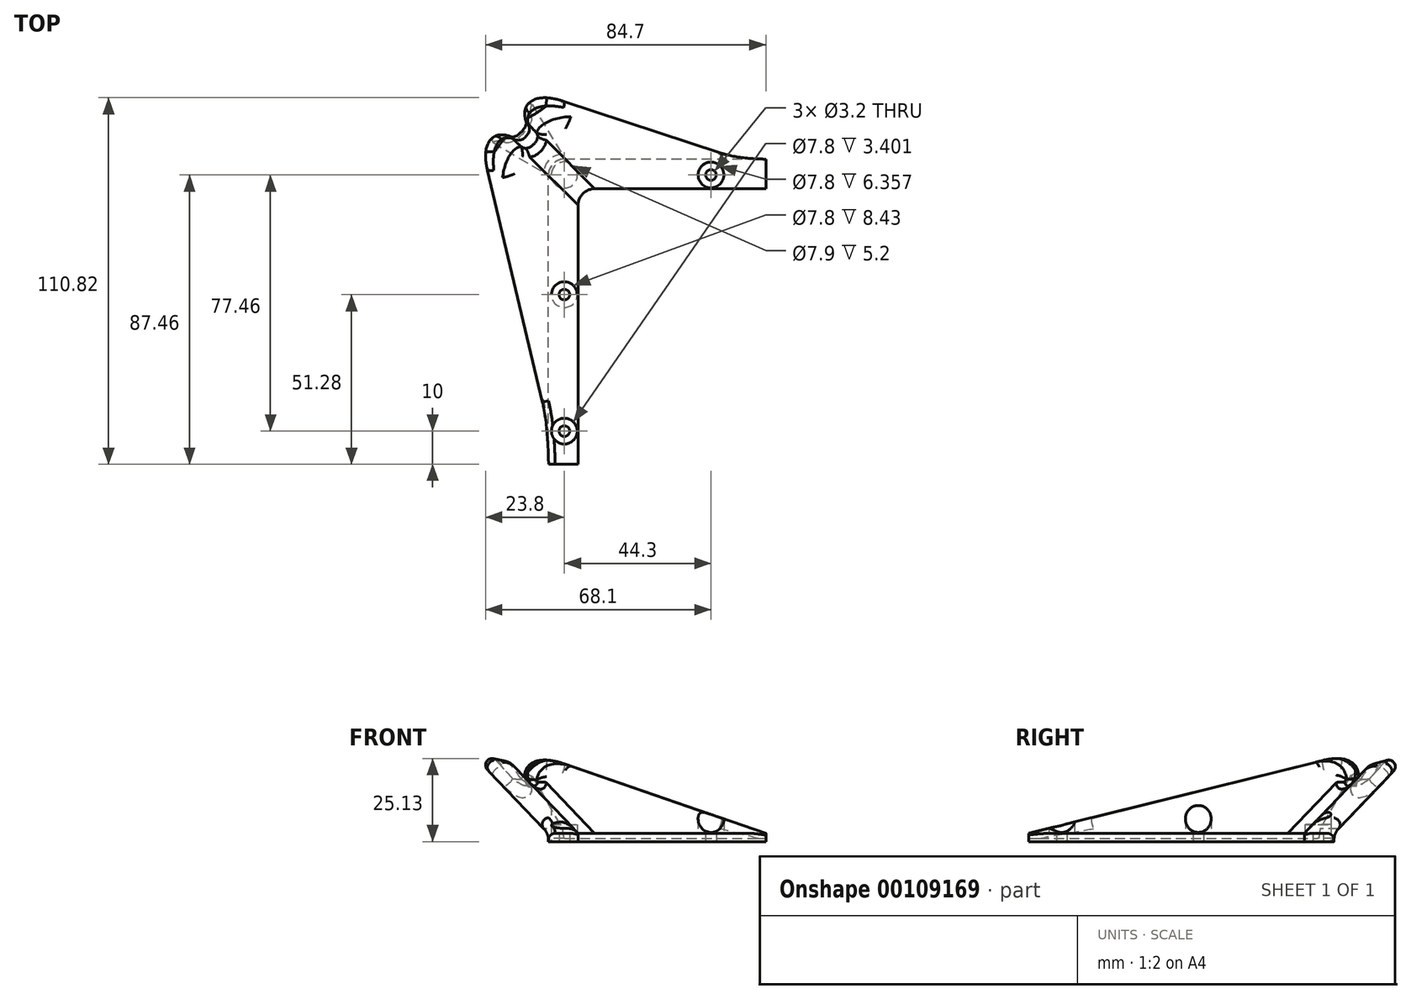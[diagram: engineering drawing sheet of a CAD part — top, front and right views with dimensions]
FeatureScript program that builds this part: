
annotation { "Feature Type Name" : "Feature", "Feature Type Description" : "" }
export const myFeature = defineFeature(function(context is Context, id is Id, definition is map)
    precondition{}
    {
        {
            var Q0;
            Q0=qCreatedBy(makeId("Top.planeOp"),FACE);
            var sketch = newSketch(context, id + "F0", { "sketchPlane" : qUnion([Q0])});
            skLineSegment(sketch, "E0", {"start": v(5, 0) * mm, "end": v(65.74, 0) * mm});
            skLineSegment(sketch, "E1", {"start": v(65.74, 0) * mm, "end": v(65.74, -9) * mm});
            skLineSegment(sketch, "E2", {"start": v(65.74, -9) * mm, "end": v(14, -9) * mm});
            skLineSegment(sketch, "E3", {"start": v(9, -14) * mm, "end": v(9, -92.3) * mm});
            skLineSegment(sketch, "E4", {"start": v(9, -92.3) * mm, "end": v(0, -92.3) * mm});
            skLineSegment(sketch, "E5", {"start": v(0, -92.3) * mm, "end": v(0, -5) * mm});
            skPoint(sketch, "E6.visualSharp", {"position": v(9, -9) * mm});
            skArc(sketch, "E6.filletArc", {"start": v(14, -9) * mm, "mid": v(10.46, -10.46) * mm, "end": v(9, -14) * mm});
            skPoint(sketch, "E7.visualSharp", {"position": v(0, 0) * mm});
            skArc(sketch, "E7.filletArc", {"start": v(5, 0) * mm, "mid": v(1.46, -1.46) * mm, "end": v(0, -5) * mm});
            skLineSegment(sketch, "E8", {"start": v(0, 0) * mm, "end": v(9, -9) * mm, "construction": true});
            skCircle(sketch, "E9", {"center": v(4.84, -4.84) * mm, "radius": 1.6 * mm});
            skCircle(sketch, "E10", {"center": v(49.14, -4.84) * mm, "radius": 1.6 * mm});
            skCircle(sketch, "E11", {"center": v(4.84, -41.02) * mm, "radius": 1.6 * mm});
            skCircle(sketch, "E12", {"center": v(4.84, -82.3) * mm, "radius": 1.6 * mm});
            skLineSegment(sketch, "E13", {"start": v(4.84, -92.3) * mm, "end": v(4.84, -4.84) * mm, "construction": true});
            skLineSegment(sketch, "E14", {"start": v(4.84, -4.84) * mm, "end": v(65.74, -4.84) * mm, "construction": true});
            skSolve(sketch);
        }
        {
            var Q0;
            Q0 = qSketchRegion(id + "F0", true);
            extrude(context, id + "F1", {"entities" : qUnion([Q0]), "depth" : 1.5 * mm});
        }
        {
            var Q0;
            Q0=qCreatedBy(makeId("Top.planeOp"),FACE);
            cPlane(context, id + "F2", {"entities" : qUnion([Q0]), "cplaneType" : CPlaneType.OFFSET, "offset" : 25 * mm, "width" : 150 * mm, "height" : 150 * mm});
        }
        {
            var Q0;
            Q0=qCreatedBy(id+"F2.planeOp",FACE);
            var sketch = newSketch(context, id + "F3", { "sketchPlane" : qUnion([Q0])});
            skLineSegment(sketch, "E15", {"start": v(0, 0) * mm, "end": v(-11.16, 11.16) * mm, "construction": true});
            skSolve(sketch);
        }
        {
            var Q0;
            Q0=makeQuery(id+"F1.opExtrude","CAP_FACE",FACE,{"disambiguationData":[OSD([sQuery(id+"F0.wireOp",EDGE,"E0"),sQuery(id+"F0.wireOp",EDGE,"E1"),sQuery(id+"F0.wireOp",EDGE,"E2"),sQuery(id+"F0.wireOp",EDGE,"E3"),sQuery(id+"F0.wireOp",EDGE,"E4"),sQuery(id+"F0.wireOp",EDGE,"E5"),sQuery(id+"F0.wireOp",EDGE,"E6.filletArc"),sQuery(id+"F0.wireOp",EDGE,"E7.filletArc"),sQuery(id+"F0.wireOp",EDGE,"E9"),sQuery(id+"F0.wireOp",EDGE,"E10"),sQuery(id+"F0.wireOp",EDGE,"E11"),sQuery(id+"F0.wireOp",EDGE,"E12")])],"isStart":false});
            var sketch = newSketch(context, id + "F4", { "sketchPlane" : qUnion([Q0])});
            skLineSegment(sketch, "E16.0", {"start": v(5, 0) * mm, "end": v(65.74, 0) * mm});
            skArc(sketch, "E16.1", {"start": v(5, 0) * mm, "mid": v(1.46, -1.46) * mm, "end": v(0, -5) * mm});
            skLineSegment(sketch, "E16.2", {"start": v(0, -92.3) * mm, "end": v(0, -5) * mm});
            skLineSegment(sketch, "E16.3", {"start": v(9, -14) * mm, "end": v(9, -92.3) * mm});
            skArc(sketch, "E16.4", {"start": v(14, -9) * mm, "mid": v(10.46, -10.46) * mm, "end": v(9, -14) * mm});
            skLineSegment(sketch, "E16.5", {"start": v(65.74, -9) * mm, "end": v(14, -9) * mm});
            skLineSegment(sketch, "E16.6", {"start": v(65.74, 0) * mm, "end": v(65.74, -9) * mm});
            skLineSegment(sketch, "E16.7", {"start": v(9, -92.3) * mm, "end": v(0, -92.3) * mm});
            skSolve(sketch);
        }
        {
            var Q0;
            Q0=qCreatedBy(id+"F2.planeOp",FACE);
            var sketch = newSketch(context, id + "F5", { "sketchPlane" : qUnion([Q0])});
            skLineSegment(sketch, "E17", {"start": v(-8.47, 13.47) * mm, "end": v(-2.47, 13.47) * mm});
            skLineSegment(sketch, "E18", {"start": v(-13.47, 8.47) * mm, "end": v(-13.47, 2.47) * mm});
            skLineSegment(sketch, "E19", {"start": v(-2.47, 22.47) * mm, "end": v(-8.47, 22.47) * mm});
            skLineSegment(sketch, "E20", {"start": v(-22.47, 8.47) * mm, "end": v(-22.47, 2.47) * mm});
            skLineSegment(sketch, "E21", {"start": v(-22.47, 2.47) * mm, "end": v(-13.47, 2.47) * mm});
            skLineSegment(sketch, "E22", {"start": v(-2.47, 22.47) * mm, "end": v(-2.47, 13.47) * mm});
            skPoint(sketch, "E23.visualSharp", {"position": v(-13.47, 13.47) * mm});
            skArc(sketch, "E23.filletArc", {"start": v(-8.47, 13.47) * mm, "mid": v(-12, 12) * mm, "end": v(-13.47, 8.47) * mm});
            skPoint(sketch, "E24.visualSharp", {"position": v(-22.47, 22.47) * mm});
            skArc(sketch, "E24.filletArc", {"start": v(-8.47, 22.47) * mm, "mid": v(-18.37, 18.37) * mm, "end": v(-22.47, 8.47) * mm});
            skSolve(sketch);
        }
        {
            var Q1;
            Q1 = qSketchRegion(id + "F5", true);
            var Q2;
            Q2 = qSketchRegion(id + "F4", true);
            loft(context, id + "F6", {"operationType" : NewBodyOperationType.ADD, "sheetProfilesArray" : [{ "sheetProfileEntities" : qUnion([Q1]) }, { "sheetProfileEntities" : qUnion([Q2]) }]});
        }
        {
            var Q0;
            Q0=makeQuery(id+"F6.opLoft","MID_CAP_EDGE",EDGE,{"disambiguationData":[OSD([sQuery(id+"F5.wireOp",EDGE,"E18"),sQuery(id+"F5.wireOp",EDGE,"E20"),sQuery(id+"F5.wireOp",EDGE,"E21")])],"capPos":0.0});
            var Q1;
            Q1=makeQuery(id+"F6.opLoft","MID_CAP_EDGE",EDGE,{"disambiguationData":[OSD([sQuery(id+"F5.wireOp",EDGE,"E17"),sQuery(id+"F5.wireOp",EDGE,"E19"),sQuery(id+"F5.wireOp",EDGE,"E22")])],"capPos":0.0});
            fillet(context, id + "F7", {"entities" : qUnion([Q0, Q1]), "radius" : 30 * mm, "tangentPropagation" : true, "allowEdgeOverflow" : false});
        }
        {
            var Q0;
            Q0=makeQuery(id+"F6.boolean.opBoolean","MERGE",EDGE,{"derivedFrom":[makeQuery(id+"F1.opExtrude","CAP_EDGE",EDGE,{"disambiguationData":[OSD([sQuery(id+"F0.wireOp",EDGE,"E5")])],"isStart":false}),makeQuery(id+"F6.opLoft","MID_CAP_EDGE",EDGE,{"disambiguationData":[OSD([sQuery(id+"F4.wireOp",EDGE,"E16.1"),sQuery(id+"F4.wireOp",EDGE,"E16.2"),sQuery(id+"F4.wireOp",EDGE,"E16.7")])],"capPos":1.0})]});
            fillet(context, id + "F8", {"entities" : qUnion([Q0]), "radius" : 5 * mm, "tangentPropagation" : true, "allowEdgeOverflow" : false});
        }
        {
            var Q0;
            Q0=sQuery(id+"F3.wireOp",EDGE,"E15");
            var Q1;
            Q1=sQuery(id+"F3.wireOp",VERTEX,"E15.end");
            cPlane(context, id + "F9", {"entities" : qUnion([Q0, Q1]), "cplaneType" : CPlaneType.LINE_POINT, "offset" : 25 * mm, "width" : 150 * mm, "height" : 150 * mm});
        }
        {
            var Q0;
            Q0=qCreatedBy(id+"F9.planeOp",FACE);
            var sketch = newSketch(context, id + "F10", { "sketchPlane" : qUnion([Q0])});
            skArc(sketch, "E25", {"start": v(-3.54, 19.4) * mm, "mid": v(0, 15.86) * mm, "end": v(3.54, 19.4) * mm});
            skLineSegment(sketch, "E26", {"start": v(3.54, 19.4) * mm, "end": v(3.54, 37.26) * mm});
            skLineSegment(sketch, "E27", {"start": v(-3.54, 19.4) * mm, "end": v(-3.54, 37.26) * mm});
            skLineSegment(sketch, "E28", {"start": v(-3.54, 37.26) * mm, "end": v(3.54, 37.26) * mm});
            skSolve(sketch);
        }
        {
            var Q0;
            Q0 = qSketchRegion(id + "F10", true);
            extrude(context, id + "F11", {"entities" : qUnion([Q0]), "operationType" : NewBodyOperationType.REMOVE, "endBound" : BoundingType.SYMMETRIC, "oppositeDirection" : true, "depth" : 25 * mm});
        }
        {
            var Q0;
            Q0=makeQuery(id+"F11.boolean.opBoolean","INTERSECT",EDGE,{"derivedFrom":[makeQuery(id+"F6.opLoft","CAP_FACE",FACE,{"disambiguationData":[OSD([makeQuery(id+"F5.imprint","IMPRINT",FACE,{"disambiguationData":[TD([[makeQuery(id+"F5.imprint","IMPRINT",EDGE,{"derivedFrom":sQuery(id+"F5.wireOp",EDGE,"E17")}),1.0]])]})])],"isStart":true}),makeQuery(id+"F11.opExtrude","SWEPT_FACE",FACE,{"disambiguationData":[OSD([sQuery(id+"F10.wireOp",EDGE,"E26")])]})]});
            var Q1;
            Q1=makeQuery(id+"F11.boolean.opBoolean","INTERSECT",EDGE,{"derivedFrom":[makeQuery(id+"F6.opLoft","CAP_FACE",FACE,{"disambiguationData":[OSD([makeQuery(id+"F5.imprint","IMPRINT",FACE,{"disambiguationData":[TD([[makeQuery(id+"F5.imprint","IMPRINT",EDGE,{"derivedFrom":sQuery(id+"F5.wireOp",EDGE,"E17")}),1.0]])]})])],"isStart":true}),makeQuery(id+"F11.opExtrude","SWEPT_FACE",FACE,{"disambiguationData":[OSD([sQuery(id+"F10.wireOp",EDGE,"E27")])]})]});
            fillet(context, id + "F12", {"entities" : qUnion([Q0, Q1]), "radius" : 10 * mm, "tangentPropagation" : true, "allowEdgeOverflow" : false});
        }
        {
            var Q0;
            Q0=makeQuery(id+"F11.boolean.opBoolean","INTERSECT",EDGE,{"derivedFrom":[makeQuery(id+"F6.opLoft","SWEPT_FACE",FACE,{"disambiguationData":[OSD([sQuery(id+"F4.wireOp",EDGE,"E16.3"),sQuery(id+"F4.wireOp",EDGE,"E16.4"),sQuery(id+"F4.wireOp",EDGE,"E16.5"),sQuery(id+"F5.wireOp",EDGE,"E17"),sQuery(id+"F5.wireOp",EDGE,"E18"),sQuery(id+"F5.wireOp",EDGE,"E23.filletArc")])]}),makeQuery(id+"F11.opExtrude","SWEPT_FACE",FACE,{"disambiguationData":[OSD([sQuery(id+"F10.wireOp",EDGE,"E25")])]})]});
            fillet(context, id + "F13", {"entities" : qUnion([Q0]), "radius" : 5 * mm, "tangentPropagation" : true, "allowEdgeOverflow" : false});
        }
        {
            var Q0;
            {var subQ0=sQuery(id+"F5.wireOp",EDGE,"E24.filletArc");var subQ1=sQuery(id+"F5.wireOp",EDGE,"E20");var subQ2=sQuery(id+"F5.wireOp",EDGE,"E19");Q0=makeQuery(id+"F12.opFillet","BLEND_EDGE",EDGE,{"blendedFrom":[makeQuery(id+"F11.boolean.opBoolean","INTERSECT",EDGE,{"derivedFrom":[makeQuery(id+"F6.opLoft","CAP_FACE",FACE,{"disambiguationData":[OSD([makeQuery(id+"F5.imprint","IMPRINT",FACE,{"disambiguationData":[TD([[makeQuery(id+"F5.imprint","IMPRINT",EDGE,{"derivedFrom":sQuery(id+"F5.wireOp",EDGE,"E17")}),1.0]])]})])],"isStart":true}),makeQuery(id+"F11.opExtrude","SWEPT_FACE",FACE,{"disambiguationData":[OSD([sQuery(id+"F10.wireOp",EDGE,"E26")])]})]}),makeQuery(id+"F6.opLoft","SWEPT_FACE",FACE,{"disambiguationData":[OSD([sQuery(id+"F4.wireOp",EDGE,"E16.0"),sQuery(id+"F4.wireOp",EDGE,"E16.1"),sQuery(id+"F4.wireOp",EDGE,"E16.2"),subQ2,subQ1,subQ0])]})],"blendedInto":[makeQuery(id+"F6.opLoft","SWEPT_FACE",FACE,{"disambiguationData":[OSD([sQuery(id+"F4.wireOp",EDGE,"E16.0"),sQuery(id+"F4.wireOp",EDGE,"E16.1"),sQuery(id+"F4.wireOp",EDGE,"E16.2"),subQ2,subQ1,subQ0])]})]});}
            fillet(context, id + "F14", {"entities" : qUnion([Q0]), "radius" : 2 * mm, "tangentPropagation" : true, "allowEdgeOverflow" : false});
        }
        {
            var Q0;
            {var subQ0=sQuery(id+"F0.wireOp",EDGE,"E12");Q0=makeQuery(id+"F6.boolean.opBoolean","SPLIT",FACE,{"disambiguationData":[TD([makeQuery(id+"F1.opExtrude","SWEPT_FACE",FACE,{"disambiguationData":[OSD([subQ0])]})])],"derivedFrom":makeQuery(id+"F6.opLoft","CAP_FACE",FACE,{"disambiguationData":[OSD([makeQuery(id+"F4.imprint","IMPRINT",FACE,{"disambiguationData":[TD([[makeQuery(id+"F4.imprint","IMPRINT",EDGE,{"derivedFrom":sQuery(id+"F4.wireOp",EDGE,"E16.0")}),-1.0]])]})])],"isStart":true})});}
            var sketch = newSketch(context, id + "F15", { "sketchPlane" : qUnion([Q0])});
            skCircle(sketch, "E29", {"center": v(4.84, 82.3) * mm, "radius": 3.9 * mm});
            skCircle(sketch, "E30", {"center": v(4.84, 41.02) * mm, "radius": 3.9 * mm});
            skCircle(sketch, "E31", {"center": v(49.14, 4.84) * mm, "radius": 3.9 * mm});
            skSolve(sketch);
        }
        {
            var Q0;
            Q0 = qSketchRegion(id + "F15", true);
            extrude(context, id + "F16", {"entities" : qUnion([Q0]), "operationType" : NewBodyOperationType.REMOVE, "oppositeDirection" : true, "depth" : 25 * mm});
        }
        {
            var Q0;
            Q0=makeQuery(id+"F1.opExtrude","CAP_FACE",FACE,{"disambiguationData":[OSD([sQuery(id+"F0.wireOp",EDGE,"E0"),sQuery(id+"F0.wireOp",EDGE,"E1"),sQuery(id+"F0.wireOp",EDGE,"E2"),sQuery(id+"F0.wireOp",EDGE,"E3"),sQuery(id+"F0.wireOp",EDGE,"E4"),sQuery(id+"F0.wireOp",EDGE,"E5"),sQuery(id+"F0.wireOp",EDGE,"E6.filletArc"),sQuery(id+"F0.wireOp",EDGE,"E7.filletArc"),sQuery(id+"F0.wireOp",EDGE,"E9"),sQuery(id+"F0.wireOp",EDGE,"E10"),sQuery(id+"F0.wireOp",EDGE,"E11"),sQuery(id+"F0.wireOp",EDGE,"E12")])],"isStart":true});
            var sketch = newSketch(context, id + "F17", { "sketchPlane" : qUnion([Q0])});
            skCircle(sketch, "E32", {"center": v(4.84, 4.84) * mm, "radius": 3.95 * mm});
            skSolve(sketch);
        }
        {
            var Q0;
            Q0 = qSketchRegion(id + "F17", true);
            extrude(context, id + "F18", {"entities" : qUnion([Q0]), "operationType" : NewBodyOperationType.REMOVE, "oppositeDirection" : true, "depth" : 4.2 * mm});
        }
        {
            var Q0;
            Q0=makeQuery(id+"F1.opExtrude","CAP_FACE",FACE,{"disambiguationData":[OSD([sQuery(id+"F0.wireOp",EDGE,"E0"),sQuery(id+"F0.wireOp",EDGE,"E1"),sQuery(id+"F0.wireOp",EDGE,"E2"),sQuery(id+"F0.wireOp",EDGE,"E3"),sQuery(id+"F0.wireOp",EDGE,"E4"),sQuery(id+"F0.wireOp",EDGE,"E5"),sQuery(id+"F0.wireOp",EDGE,"E6.filletArc"),sQuery(id+"F0.wireOp",EDGE,"E7.filletArc"),sQuery(id+"F0.wireOp",EDGE,"E9"),sQuery(id+"F0.wireOp",EDGE,"E10"),sQuery(id+"F0.wireOp",EDGE,"E11"),sQuery(id+"F0.wireOp",EDGE,"E12")])],"isStart":true});
            extrude(context, id + "F19", {"entities" : qUnion([Q0]), "operationType" : NewBodyOperationType.ADD, "depth" : 1 * mm});
        }
    });
